# Revit family: 203_2188caf4c3d94120a093f4b1cd3702
name_source: partatom
category: Duct Accessories
revit_build: Autodesk Revit 2018 (Build: 20170223_1515(x64)
units: mm (PartAtom-declared; Revit-internal decimal feet)

## family parameters
Always vertical = Yes
Cut with Voids When Loaded = No
Part Type = Damper
Round Connector Dimension = Use Diameter
Shared = No
Work Plane-Based = No

## types (7) — shared parameters
AH = 75 mm  [stored 0.246063 ft]
AL = 60 mm  [stored 0.19685 ft]
ALT2 = 30 mm  [stored 0.0984252 ft]
APL = 70 mm  [stored 0.229659 ft]
APLT2 = 35 mm  [stored 0.114829 ft]
CAT0 = Yes
D3 = 30 mm  [stored 0.0984252 ft]
Description = Closing air damper w/spring
H1 = 45 mm
H1__ve = -45 mm  [stored -0.147638 ft]
H2D = 125 mm  [stored 0.410105 ft]
L2D = 100 mm  [stored 0.328084 ft]
Manufacturer = Flexit
QmdConnectorList = 201;D;202;D
URL = www.flexit.no
W2D = 125 mm  [stored 0.410105 ft]
X = 25 mm  [stored 0.082021 ft]
X1 = 21 mm  [stored 0.0688976 ft]
X1__ve = -21 mm  [stored -0.0688976 ft]
X__ve = -25 mm  [stored -0.082021 ft]
Y1 = 2 mm  [stored 0.00656168 ft]
Y1__ve = -2 mm  [stored -0.00656168 ft]
Y2 = 10 mm  [stored 0.0328084 ft]
Y2__ve = -10 mm  [stored -0.0328084 ft]
Y3 = 18 mm  [stored 0.0590551 ft]
Y4 = 5 mm  [stored 0.0164042 ft]
Y4__ve = -5 mm  [stored -0.0164042 ft]
magiPartTypeId = 203
magiProductFamilyId = 2188caf4c3d94120a093f4b1cd3702

## per-type parameters (varying)
| type | APH | CD | CZONF__ve | Clearance Zone Front Depth | D | DT2 | L | LT2 | magiProductId |
| 125-111801 | 135 mm  [stored 0.442913 ft] | 125 mm  [stored 0.410105 ft] | -137 mm | 137 mm | 125 mm | 63 mm | 100 mm  [stored 0.328084 ft] | 50 mm  [stored 0.164042 ft] | ce2c7602105d43559e979750414cf2 |
| 160-14482 | 170 mm | 160 mm | -167 mm | 167 mm | 160 mm | 80 mm  [stored 0.262467 ft] | 100 mm  [stored 0.328084 ft] | 50 mm  [stored 0.164042 ft] | a04f8af7cfe24a6396ca8f43c599dd |
| 200-14481 | 210 mm | 200 mm  [stored 0.656168 ft] | -187 mm | 187 mm | 200 mm | 100 mm  [stored 0.328084 ft] | 100 mm  [stored 0.328084 ft] | 50 mm  [stored 0.164042 ft] | 03a6047ec1f644c3b98e335178314c |
| 250-14485 | 260 mm | 250 mm | -212 mm | 212 mm | 250 mm | 125 mm  [stored 0.410105 ft] | 100 mm  [stored 0.328084 ft] | 50 mm  [stored 0.164042 ft] | d3e10bb1b526400ebfaa4982e07668 |
| 315-14478 | 325 mm | 315 mm | -245 mm | 245 mm | 315 mm | 158 mm | 100 mm  [stored 0.328084 ft] | 50 mm  [stored 0.164042 ft] | b09f4dc1239e40ffa4f3e1b59b2ff6 |
| 400-14480 | 410 mm | 400 mm | -287 mm | 287 mm | 400 mm | 200 mm  [stored 0.656168 ft] | 100 mm  [stored 0.328084 ft] | 50 mm  [stored 0.164042 ft] | c9a8af046de246a984f226f0818e09 |
| 500-14440 | 510 mm | 500 mm | -337 mm  [stored -1.10564 ft] | 337 mm | 500 mm | 250 mm | 115 mm  [stored 0.377297 ft] | 58 mm | 5b1e2383daef4f6dab21d2dd80b515 |

note: column(s) folded — value = type name in every type: MC Product Code

note: [stored X ft] marks values corroborated as IEEE doubles in the binary element streams (Revit-internal decimal feet)

## geometry (parser evidence)
native form markers: Sweep x3
no freeform markers — native parametric forms only
